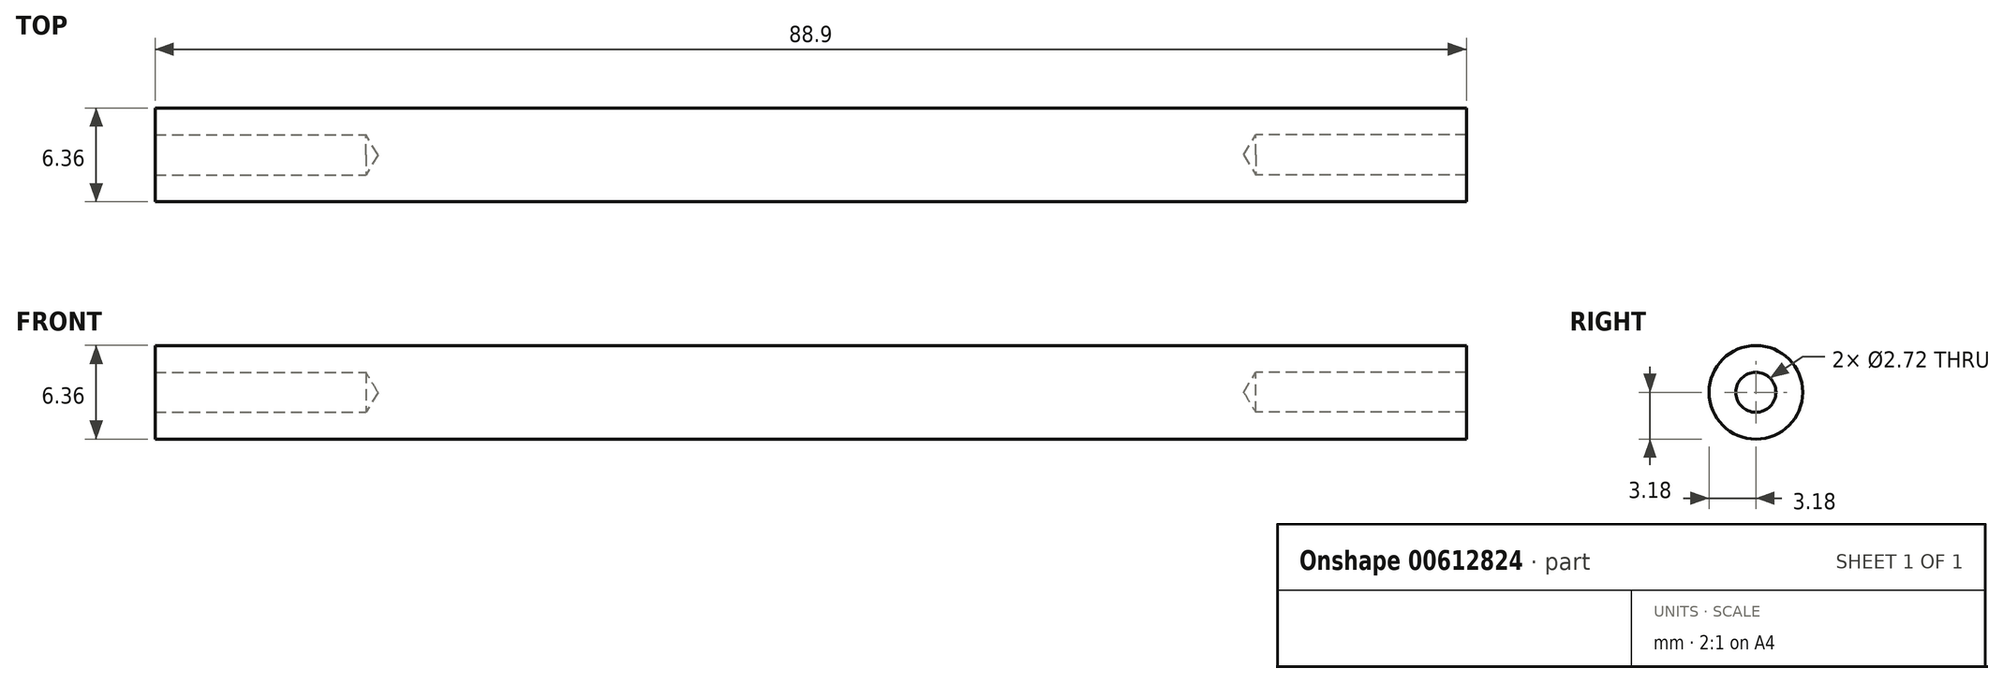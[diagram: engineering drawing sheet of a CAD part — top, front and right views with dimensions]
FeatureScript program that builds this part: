
annotation { "Feature Type Name" : "Feature", "Feature Type Description" : "" }
export const myFeature = defineFeature(function(context is Context, id is Id, definition is map)
    precondition{}
    {
        {
            var Q0;
            Q0=qCreatedBy(makeId("Right.planeOp"),FACE);
            var sketch = newSketch(context, id + "F0", { "sketchPlane" : qUnion([Q0])});
            skCircle(sketch, "E0", {"center": v(0, 0) * mm, "radius": 3.18 * mm});
            skSolve(sketch);
        }
        {
            var Q0;
            Q0=qSketchRegion(id+"F0",true);
            extrude(context, id + "F1", {"entities" : qUnion([Q0]), "depth" : 88.9 * mm, "symmetric" : true});
        }
        {
            var Q0;
            Q0=makeQuery(id+"F1.opExtrude","CAP_FACE",FACE,{"disambiguationData":[OSD([sQuery(id+"F0.wireOp",EDGE,"E0")])],"isStart":false});
            var sketch = newSketch(context, id + "F2", { "sketchPlane" : qUnion([Q0])});
            skPoint(sketch, "E1", {"position": v(0, 0) * mm});
            skSolve(sketch);
        }
        {
            var Q0;
            Q0=makeQuery(id+"F1.opExtrude","CAP_FACE",FACE,{"disambiguationData":[OSD([sQuery(id+"F0.wireOp",EDGE,"E0")])],"isStart":true});
            var sketch = newSketch(context, id + "F3", { "sketchPlane" : qUnion([Q0])});
            skPoint(sketch, "E2", {"position": v(0, 0) * mm});
            skSolve(sketch);
        }
        {
            var Q0;
            Q0=sQuery(id+"F3.wireOp",VERTEX,"E2");
            var Q1;
            Q1=sQuery(id+"F2.wireOp",VERTEX,"E1");
            var Q2;
            Q2=makeQuery(id+"F1.opExtrude","SWEPT_BODY",BODY,{"disambiguationData":[OSD([sQuery(id+"F0.wireOp",EDGE,"E0")])]});
            hole(context, id + "F4", {"style" : HoleStyle.SIMPLE, "holeDiameter" : 2.72 * mm, "endStyle" : HoleEndStyle.BLIND, "holeDepth" : 14.29 * mm, "locations" : qUnion([Q0, Q1]), "scope" : qUnion([Q2])});
        }
    });
